# Revit family: POT-201_RFA
name_source: partatom
category: Aparatos sanitarios
units: mm (PartAtom-declared; Revit-internal decimal feet)

## family parameters
Activar corte en vistas = No
Compartido = Sí
Corte con vacíos al cargar = No
Cota de conector redondo = Usar diámetro
Mantener orientación de anotación = No
Número OmniClass = 23.45.05.14.99
Punto de cálculo de habitación = Sí
Se basa en plano de trabajo = Sí
Siempre vertical = Sí
Tipo de pieza = Normal
Título OmniClass = Other Sanitary Washing Plumbing Fixtures

## types (1)
- POT-201
    Accesorios = Llave allen 2.5 mm.
    Alto = 7"
    Ancho = 5"
    Características = Monomando para regadera, tina o regadera 
manual con desviador. Con cartucho 
cerámico de 35 mm.
    Descripción = Monomando para Regadera con Desviador
    Elevación por defecto = 47"
    Fabricante = HELVEX S.A. DE C.V.
    Imagen de tipo = <Ninguno>
    Instalación = Conexión interna de 1/2"-14 NPT para agua fría (azul). Conexión interna de 1/2"-14 NPT para agua caliente (rojo). Conexión interna de 1/2"-14 NPT de salida (negro).
    Material = Brass
    Modelo = POT-201
    Operación = Para abrir el flujo de agua levante la palanca
y para cerrar empuje la palanca. Para ajustar 
la temperatura del agua, gire a la izquierda para 
caliente y gire a la derecha para fría.
    Presión máxima de trabajo = 85.3 psi
    Presión mínima de trabajo = 11.4 psi
    Profundidad = 5"

## geometry (parser evidence)
native form markers: Sweep x3
no freeform markers — native parametric forms only
